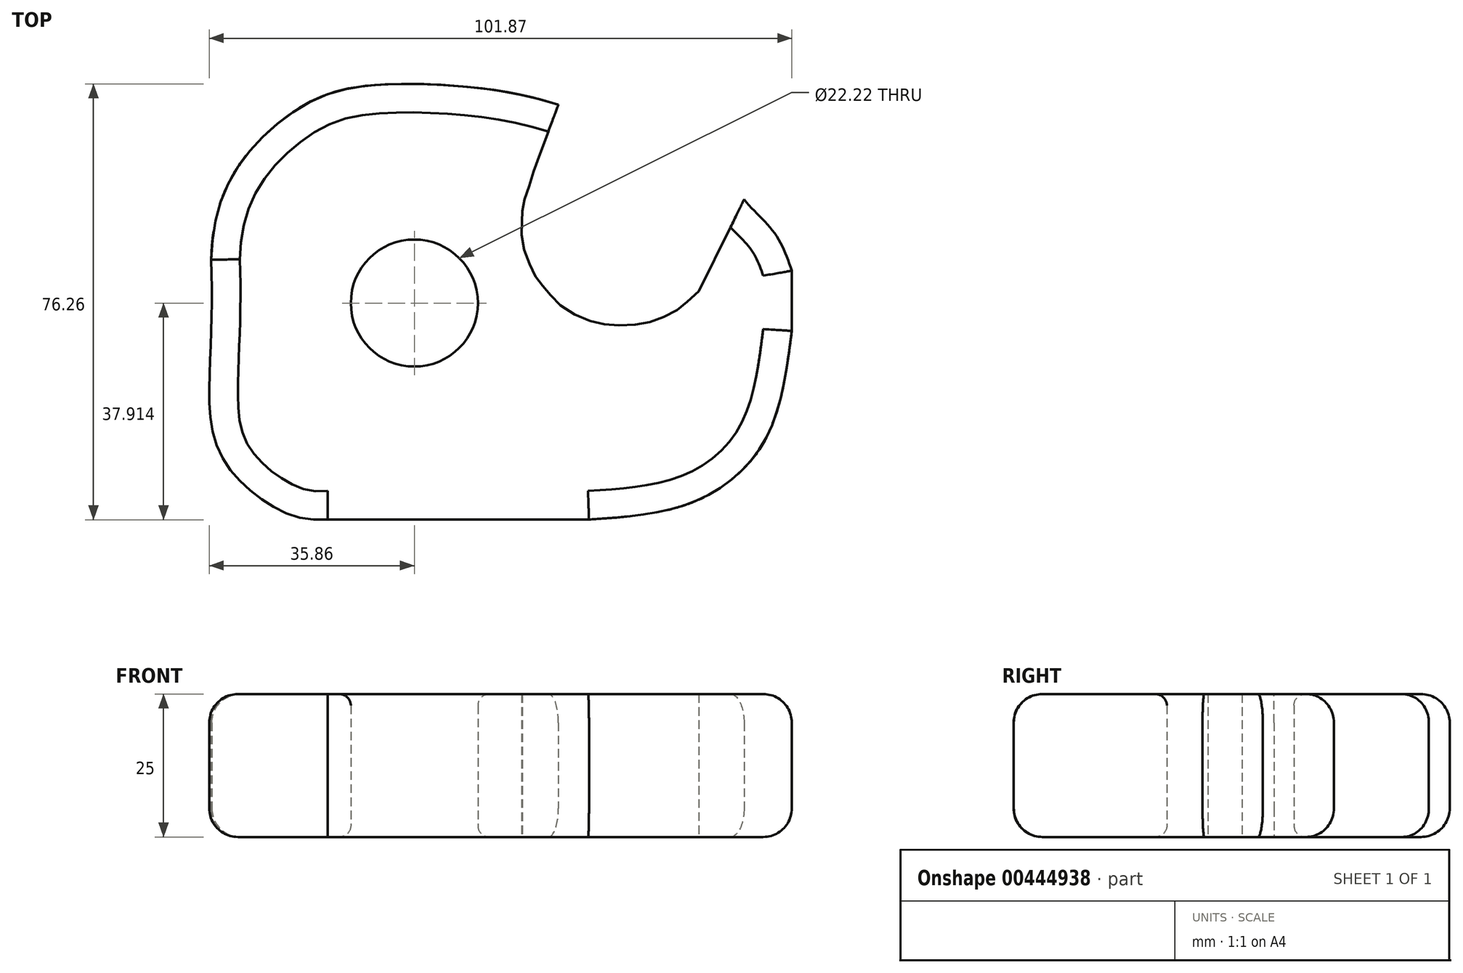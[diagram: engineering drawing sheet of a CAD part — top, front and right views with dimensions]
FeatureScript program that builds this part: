
annotation { "Feature Type Name" : "Feature", "Feature Type Description" : "" }
export const myFeature = defineFeature(function(context is Context, id is Id, definition is map)
    precondition{}
    {
        {
            var Q0;
            Q0=qCreatedBy(makeId("Top.planeOp"),FACE);
            var sketch = newSketch(context, id + "F0", { "sketchPlane" : qUnion([Q0])});
            skFitSpline(sketch, "E0", {"points": [v(16.88, 16.59) * mm, v(0, 19.8) * mm, v(-17.5, 19.8) * mm, v(-27.99, 16.28) * mm, v(-39.01, 5.94) * mm, v(-43.84, -10.52) * mm], "startDerivative": vector(-85.16, 26.88) * mm, "endDerivative": vector(-1.6, -93) * mm});
            skFitSpline(sketch, "E1", {"points": [v(-43.84, -10.52) * mm, v(-42.14, -44.72) * mm, v(-29.82, -55.25) * mm, v(-23.44, -56) * mm], "startDerivative": vector(4.22, -110.94) * mm, "endDerivative": vector(28.41, 0.63) * mm});
            skFitSpline(sketch, "E2", {"points": [v(-23.44, -56) * mm, v(22.22, -56) * mm], "startDerivative": vector(45.67, 0) * mm, "endDerivative": vector(45.67, 0) * mm});
            skFitSpline(sketch, "E3", {"points": [v(22.22, -56) * mm, v(40.34, -52.97) * mm, v(52.86, -42.32) * mm, v(57.69, -23) * mm], "startDerivative": vector(56.44, 3.74) * mm, "endDerivative": vector(7.7, 59.84) * mm});
            skFitSpline(sketch, "E4", {"points": [v(57.69, -23) * mm, v(57.69, -12.45) * mm], "startDerivative": vector(0, 10.54) * mm, "endDerivative": vector(0, 10.54) * mm});
            skFitSpline(sketch, "E5", {"points": [v(57.69, -12.45) * mm, v(54.72, -5.97) * mm, v(49.34, 0) * mm], "startDerivative": vector(-5.06, 13.79) * mm, "endDerivative": vector(-8.31, 10.5) * mm});
            skFitSpline(sketch, "E6", {"points": [v(49.34, 0) * mm, v(41.44, -16.08) * mm], "startDerivative": vector(-7.9, -16.08) * mm, "endDerivative": vector(-7.9, -16.08) * mm});
            skFitSpline(sketch, "E7", {"points": [v(41.44, -16.08) * mm, v(38.4, -18.78) * mm, v(34.89, -20.76) * mm, v(30.93, -21.85) * mm, v(26.2, -21.97) * mm, v(22.37, -21.2) * mm, v(17.5, -18.78) * mm, v(14.95, -16.08) * mm, v(13.23, -14.05) * mm, v(11.7, -11.05) * mm, v(10.48, -6.83) * mm, v(10.54, -3.38) * mm, v(10.6, -1.47) * mm, v(11.57, 1.86) * mm, v(13.04, 6.27) * mm, v(16.88, 16.59) * mm], "startDerivative": vector(-65.47, -53.27) * mm, "endDerivative": vector(40.1, 105.32) * mm});
            skCircle(sketch, "E8", {"center": v(-8.32, -18.12) * mm, "radius": 11.11 * mm});
            skSolve(sketch);
        }
        {
            var Q0;
            Q0=makeQuery(id+"F0.imprint","IMPRINT",FACE,{"disambiguationData":[TD([[makeQuery(id+"F0.imprint","IMPRINT",EDGE,{"derivedFrom":sQuery(id+"F0.wireOp",EDGE,"E0")}),1.0]])]});
            extrude(context, id + "F1", {"entities" : qUnion([Q0]), "depth" : 25 * mm});
        }
        {
            var Q0;
            Q0=makeQuery(id+"F1.opExtrude","CAP_EDGE",EDGE,{"disambiguationData":[OSD([sQuery(id+"F0.wireOp",EDGE,"E0")])],"isStart":false});
            var Q1;
            Q1=makeQuery(id+"F1.opExtrude","CAP_EDGE",EDGE,{"disambiguationData":[OSD([sQuery(id+"F0.wireOp",EDGE,"E1")])],"isStart":false});
            var Q2;
            Q2=makeQuery(id+"F1.opExtrude","CAP_EDGE",EDGE,{"disambiguationData":[OSD([sQuery(id+"F0.wireOp",EDGE,"E2")])],"isStart":false});
            var Q3;
            Q3=makeQuery(id+"F1.opExtrude","CAP_EDGE",EDGE,{"disambiguationData":[OSD([sQuery(id+"F0.wireOp",EDGE,"E3")])],"isStart":false});
            var Q4;
            Q4=makeQuery(id+"F1.opExtrude","CAP_EDGE",EDGE,{"disambiguationData":[OSD([sQuery(id+"F0.wireOp",EDGE,"E4")])],"isStart":false});
            var Q5;
            Q5=makeQuery(id+"F1.opExtrude","CAP_EDGE",EDGE,{"disambiguationData":[OSD([sQuery(id+"F0.wireOp",EDGE,"E5")])],"isStart":false});
            fillet(context, id + "F2", {"entities" : qUnion([Q0, Q1, Q2, Q3, Q4, Q5]), "radius" : 5 * mm, "tangentPropagation" : true, "allowEdgeOverflow" : false});
        }
        {
            var Q0;
            Q0=makeQuery(id+"F1.opExtrude","CAP_EDGE",EDGE,{"disambiguationData":[OSD([sQuery(id+"F0.wireOp",EDGE,"E0")])],"isStart":true});
            var Q1;
            Q1=makeQuery(id+"F1.opExtrude","CAP_EDGE",EDGE,{"disambiguationData":[OSD([sQuery(id+"F0.wireOp",EDGE,"E2")])],"isStart":true});
            var Q2;
            Q2=makeQuery(id+"F1.opExtrude","CAP_EDGE",EDGE,{"disambiguationData":[OSD([sQuery(id+"F0.wireOp",EDGE,"E1")])],"isStart":true});
            var Q3;
            Q3=makeQuery(id+"F1.opExtrude","CAP_EDGE",EDGE,{"disambiguationData":[OSD([sQuery(id+"F0.wireOp",EDGE,"E3")])],"isStart":true});
            var Q4;
            Q4=makeQuery(id+"F1.opExtrude","CAP_EDGE",EDGE,{"disambiguationData":[OSD([sQuery(id+"F0.wireOp",EDGE,"E5")])],"isStart":true});
            var Q5;
            Q5=makeQuery(id+"F1.opExtrude","CAP_EDGE",EDGE,{"disambiguationData":[OSD([sQuery(id+"F0.wireOp",EDGE,"E4")])],"isStart":true});
            fillet(context, id + "F3", {"entities" : qUnion([Q0, Q1, Q2, Q3, Q4, Q5]), "radius" : 5 * mm, "tangentPropagation" : true, "allowEdgeOverflow" : false});
        }
        {
            var Q0;
            Q0=makeQuery(id+"F1.opExtrude","CAP_EDGE",EDGE,{"disambiguationData":[OSD([sQuery(id+"F0.wireOp",EDGE,"E8")])],"isStart":false});
            fillet(context, id + "F4", {"entities" : qUnion([Q0]), "radius" : 2 * mm, "tangentPropagation" : true, "allowEdgeOverflow" : false});
        }
        {
            var Q0;
            Q0=makeQuery(id+"F1.opExtrude","CAP_EDGE",EDGE,{"disambiguationData":[OSD([sQuery(id+"F0.wireOp",EDGE,"E8")])],"isStart":true});
            fillet(context, id + "F5", {"entities" : qUnion([Q0]), "radius" : 2 * mm, "tangentPropagation" : true, "allowEdgeOverflow" : false});
        }
    });
